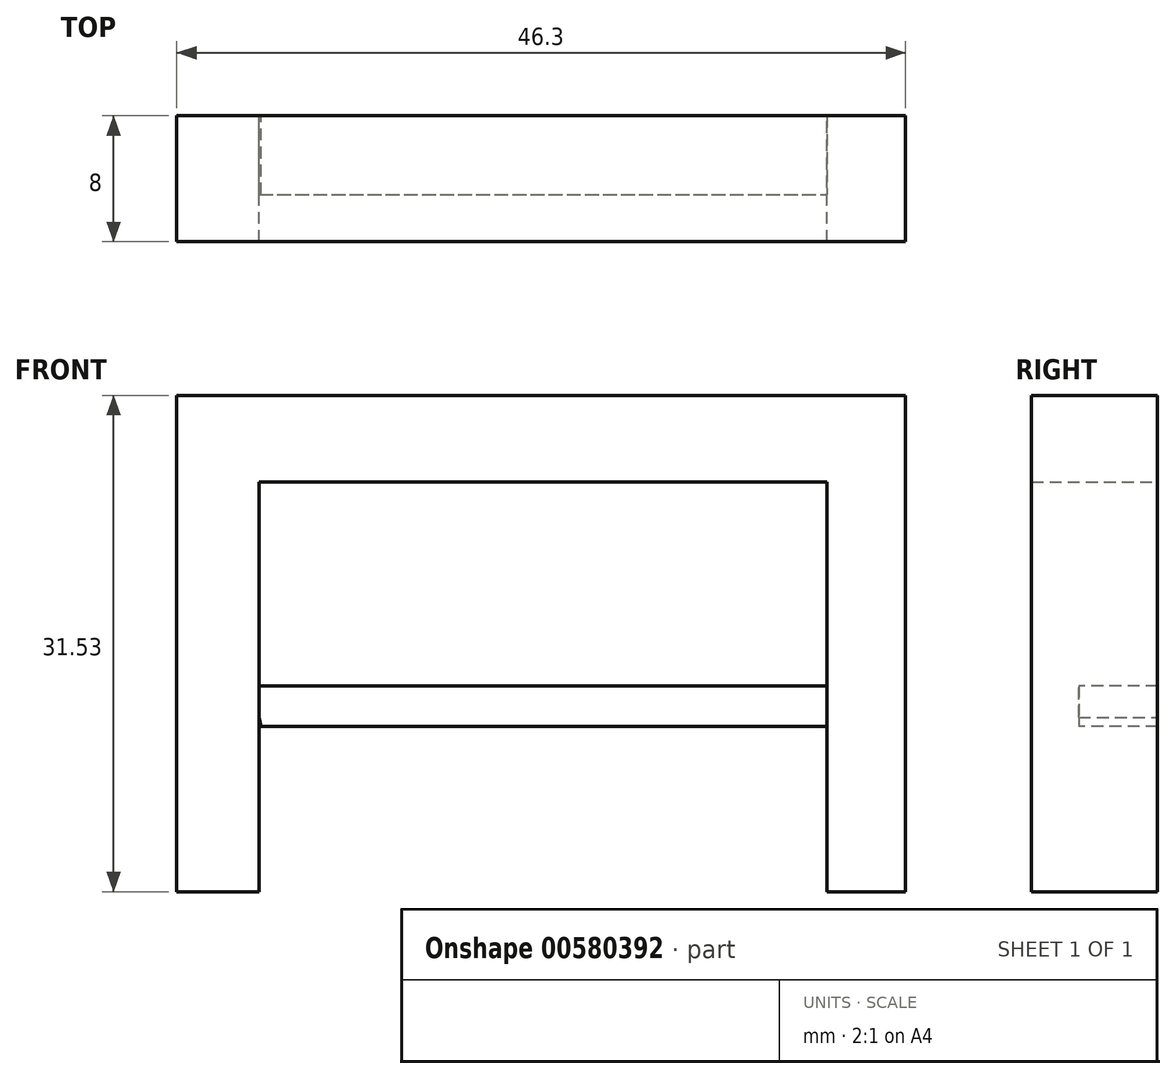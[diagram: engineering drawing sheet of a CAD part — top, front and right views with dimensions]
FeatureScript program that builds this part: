
annotation { "Feature Type Name" : "Feature", "Feature Type Description" : "" }
export const myFeature = defineFeature(function(context is Context, id is Id, definition is map)
    precondition{}
    {
        {
            var Q0;
            Q0=qCreatedBy(makeId("Front.planeOp"),FACE);
            var sketch = newSketch(context, id + "F0", { "sketchPlane" : qUnion([Q0])});
            skLineSegment(sketch, "E0", {"start": v(-58.51, 0) * mm, "end": v(-58.51, 31.53) * mm});
            skLineSegment(sketch, "E1", {"start": v(-58.51, 31.53) * mm, "end": v(-12.2, 31.53) * mm});
            skLineSegment(sketch, "E2", {"start": v(-12.2, 31.53) * mm, "end": v(-12.2, 0) * mm});
            skLineSegment(sketch, "E3", {"start": v(-58.51, 0) * mm, "end": v(-53.28, 0) * mm});
            skLineSegment(sketch, "E4", {"start": v(-53.28, 0) * mm, "end": v(-53.28, 26.02) * mm});
            skLineSegment(sketch, "E5", {"start": v(-53.28, 26.02) * mm, "end": v(-17.2, 26.02) * mm});
            skLineSegment(sketch, "E6", {"start": v(-17.2, 26.02) * mm, "end": v(-17.2, 0) * mm});
            skLineSegment(sketch, "E7", {"start": v(-17.2, 0) * mm, "end": v(-12.2, 0) * mm});
            skSolve(sketch);
        }
        {
            var Q0;
            Q0 = qSketchRegion(id + "F0", true);
            extrude(context, id + "F1", {"entities" : qUnion([Q0]), "depth" : 8 * mm, "offsetDistance" : 25 * mm});
        }
        {
            var Q0;
            Q0=qCreatedBy(makeId("Front.planeOp"),FACE);
            var sketch = newSketch(context, id + "F2", { "sketchPlane" : qUnion([Q0])});
            skLineSegment(sketch, "E8", {"start": v(-52.73, 13.08) * mm, "end": v(-17.03, 13.08) * mm});
            skLineSegment(sketch, "E9", {"start": v(-53.15, 10.51) * mm, "end": v(-17.12, 10.51) * mm});
            skLineSegment(sketch, "E10", {"start": v(-17.12, 10.51) * mm, "end": v(-17.03, 13.08) * mm});
            skLineSegment(sketch, "E11", {"start": v(-52.73, 13.08) * mm, "end": v(-53.76, 13.08) * mm});
            skLineSegment(sketch, "E12", {"start": v(-53.76, 13.08) * mm, "end": v(-53.15, 10.51) * mm});
            skSolve(sketch);
        }
        {
            var Q0;
            Q0 = qSketchRegion(id + "F2", true);
            extrude(context, id + "F3", {"entities" : qUnion([Q0]), "operationType" : NewBodyOperationType.ADD, "depth" : 5 * mm, "offsetDistance" : 25 * mm});
        }
    });
